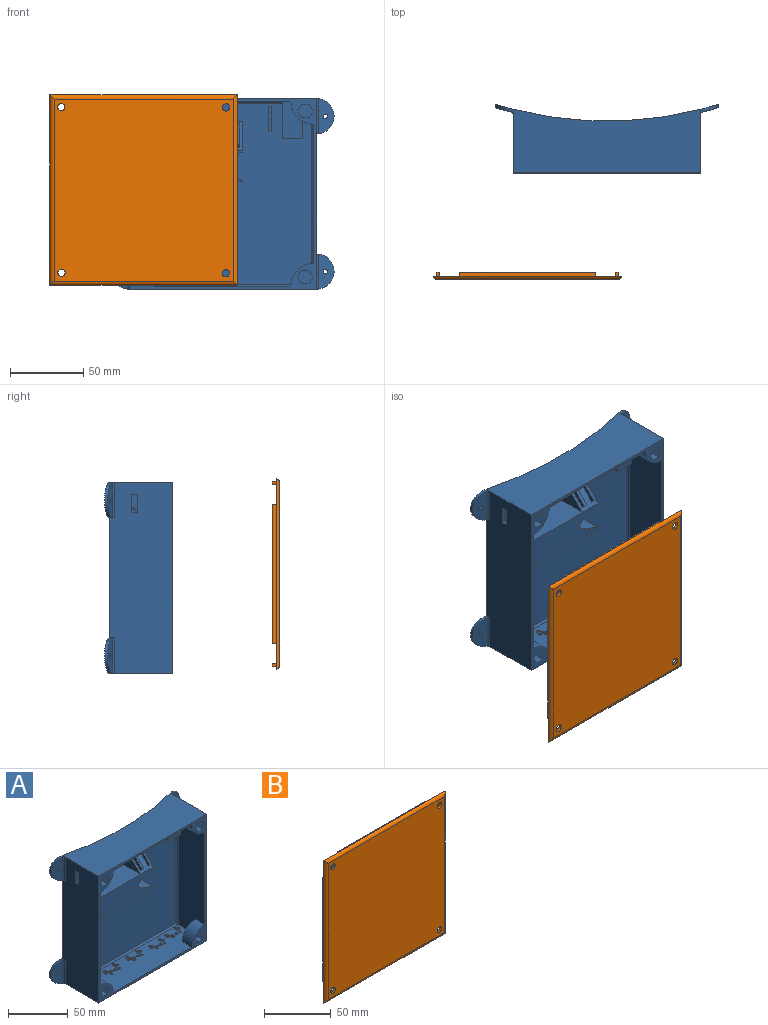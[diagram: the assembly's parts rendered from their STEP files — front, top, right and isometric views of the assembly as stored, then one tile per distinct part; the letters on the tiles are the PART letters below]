
ASSEMBLY  parts=2 mates=1
PART A: 159 faces, bbox 152x46.7x130 mm
  f0: plane 126x31.5mm, normal (1,0,0), area 3564.5mm2, adj f8,f10,f11,f21,f35,f36,f39,f40
  f1: plane 130x43.3mm, normal (-1,0,0), area 5426.5mm2, adj f8,f12,f13,f14,f17,f25,f31,f34
  f2: plane 70x21mm, normal (0,-1,0), area 1246mm2, adj f3,f130,f131,f132,f133,f137,f139
  f3: plane 21.01x20mm, normal (1,0,0), area 220mm2, adj f2,f4,f6,f136,f137,f139
  f4: plane 69x19mm, normal (0,0,-1), area 1310.4mm2, adj f3,f5,f6,f134,f136,f137
  f5: plane 69x19.04mm, normal (0,1,0), area 1087mm2, adj f4,f133,f134,f135,f137
  f6: plane 123x121mm, normal (0,-1,0), area 14390mm2, adj f3,f4,f21,f22,f23,f24,f125,f126
  f7: plane 130x43.3mm, normal (1,0,0), area 5424.5mm2, adj f8,f12,f13,f14,f15,f26,f29,f30
  f8: plane 130x128mm, normal (0,-1,0), area 1478.8mm2, adj f0,f1,f7,f9,f10,f11,f12,f13
  f9: plane 126x31.5mm, normal (-1,0,0), area 3577.1mm2, adj f8,f10,f11,f24,f37,f38,f41,f42
  f10: plane 124x31.5mm, normal (0,0,1), area 3271.1mm2, adj f0,f8,f9,f23,f39,f40,f41,f42
  f11: plane 124x31.5mm, normal (0,0,-1), area 3507.5mm2, adj f0,f8,f9,f22,f35,f36,f37,f38
  f12: plane 128x43.3mm, normal (0,0,1), area 4849.1mm2, adj f1,f7,f8,f14,f15,f17
  f13: plane 128x43.3mm, normal (0,0,-1), area 4849.1mm2, adj f1,f7,f8,f14,f30,f31
  f14: cylinder r=256.8mm len=152mm, axis (0,0,-1), area 17727.9mm2, adj f1,f7,f12,f13,f15,f17,f19,f20
  f15: cylinder r=12mm len=24mm, axis (0,1,0), area 79mm2, adj f7,f12,f14,f16,f26
  f16: cylinder r=258.8mm len=23.89mm, axis (0,0,-1), area 199.6mm2, adj f15,f19,f26
  f17: cylinder r=12mm len=24mm, axis (0,1,0), area 79mm2, adj f1,f12,f14,f18,f25
  f18: cylinder r=258.8mm len=23.89mm, axis (0,0,-1), area 199.6mm2, adj f17,f20,f25
  f19: cylinder r=1.5mm len=3mm, axis (0,1,0), area 19.6mm2, adj f14,f16
  f20: cylinder r=1.5mm len=3mm, axis (0,1,0), area 19.6mm2, adj f14,f18
  f21: cylinder r=1.5mm len=126mm, axis (0,0,1), area 294.3mm2, adj f0,f6,f22,f23
  f22: cylinder r=1.5mm len=124mm, axis (1,0,0), area 289.6mm2, adj f6,f11,f21,f24
  f23: cylinder r=1.5mm len=124mm, axis (-1,0,0), area 289.6mm2, adj f6,f10,f21,f24
  f24: cylinder r=1.5mm len=126mm, axis (0,0,-1), area 274.1mm2, adj f6,f9,f22,f23,f122,f123,f124
  f25: cylinder r=1.5mm len=24mm, axis (0,0,-1), area 47.3mm2, adj f1,f17,f18
  f26: cylinder r=1.5mm len=24mm, axis (0,0,-1), area 47.3mm2, adj f7,f15,f16
  f27: cylinder r=258.8mm len=23.89mm, axis (0,0,-1), area 199.6mm2, adj f28,f29,f30
  f28: cylinder r=1.5mm len=3mm, axis (0,1,0), area 19.6mm2, adj f14,f27
  f29: cylinder r=1.5mm len=24mm, axis (0,0,-1), area 47.3mm2, adj f7,f27,f30
  f30: cylinder r=12mm len=24mm, axis (0,1,0), area 79mm2, adj f7,f13,f14,f27,f29
  f31: cylinder r=12mm len=24mm, axis (0,1,0), area 79mm2, adj f1,f13,f14,f32,f34
  f32: cylinder r=258.8mm len=23.89mm, axis (0,0,-1), area 199.6mm2, adj f31,f33,f34
  f33: cylinder r=1.5mm len=3mm, axis (0,1,0), area 19.6mm2, adj f14,f32
  f34: cylinder r=1.5mm len=24mm, axis (0,0,-1), area 47.3mm2, adj f1,f31,f32
  f35: cylinder r=15.5mm len=15.5mm, axis (0,-1,0), area 280mm2, adj f0,f8,f11,f36
  f36: plane 15.5x15.5mm, normal (0,1,0), area 188.7mm2, adj f0,f11,f35
  f37: cylinder r=15.5mm len=15.5mm, axis (0,-1,0), area 280mm2, adj f8,f9,f11,f38
  f38: plane 15.5x15.5mm, normal (0,1,0), area 188.7mm2, adj f9,f11,f37
  f39: cylinder r=15.5mm len=15.5mm, axis (0,-1,0), area 280mm2, adj f0,f8,f10,f40
  f40: plane 15.5x15.5mm, normal (0,1,0), area 188.7mm2, adj f0,f10,f39
  f41: cylinder r=15.5mm len=15.5mm, axis (0,-1,0), area 280mm2, adj f8,f9,f10,f42
  f42: plane 15.5x15.5mm, normal (0,1,0), area 188.7mm2, adj f9,f10,f41
  f43: plane 9x5.3mm, normal (0,0,-1), area 47.7mm2, adj f8,f44,f48,f49
  f44: plane 9x4.59mm, normal (0.87,0,-0.5), area 47.7mm2, adj f8,f43,f45,f49
  f45: plane 9x4.59mm, normal (0.87,0,0.5), area 47.7mm2, adj f8,f44,f46,f49
  f46: plane 9x5.3mm, normal (0,0,1), area 47.7mm2, adj f8,f45,f47,f49
  f47: plane 9x4.59mm, normal (-0.87,0,0.5), area 47.7mm2, adj f8,f46,f48,f49
  f48: plane 9x4.59mm, normal (-0.87,0,-0.5), area 47.7mm2, adj f8,f43,f47,f49
  f49: plane 10.6x9.18mm, normal (0,-1,0), area 73mm2, adj f43,f44,f45,f46,f47,f48
  f50: plane 9x5.3mm, normal (0,0,-1), area 47.7mm2, adj f8,f51,f55,f56
  f51: plane 9x4.59mm, normal (0.87,0,-0.5), area 47.7mm2, adj f8,f50,f52,f56
  f52: plane 9x4.59mm, normal (0.87,0,0.5), area 47.7mm2, adj f8,f51,f53,f56
  f53: plane 9x5.3mm, normal (0,0,1), area 47.7mm2, adj f8,f52,f54,f56
  f54: plane 9x4.59mm, normal (-0.87,0,0.5), area 47.7mm2, adj f8,f53,f55,f56
  f55: plane 9x4.59mm, normal (-0.87,0,-0.5), area 47.7mm2, adj f8,f50,f54,f56
  f56: plane 10.6x9.18mm, normal (0,-1,0), area 73mm2, adj f50,f51,f52,f53,f54,f55
  f57: plane 9x4.59mm, normal (0.87,0,-0.5), area 47.7mm2, adj f8,f58,f62,f63
  f58: plane 9x4.59mm, normal (0.87,0,0.5), area 47.7mm2, adj f8,f57,f59,f63
  f59: plane 9x5.3mm, normal (0,0,1), area 47.7mm2, adj f8,f58,f60,f63
  f60: plane 9x4.59mm, normal (-0.87,0,0.5), area 47.7mm2, adj f8,f59,f61,f63
  f61: plane 9x4.59mm, normal (-0.87,0,-0.5), area 47.7mm2, adj f8,f60,f62,f63
  f62: plane 9x5.3mm, normal (0,0,-1), area 47.7mm2, adj f8,f57,f61,f63
  f63: plane 10.6x9.18mm, normal (0,-1,0), area 73mm2, adj f57,f58,f59,f60,f61,f62
  f64: plane 9x4.59mm, normal (0.87,0,-0.5), area 47.7mm2, adj f8,f65,f69,f70
  f65: plane 9x4.59mm, normal (0.87,0,0.5), area 47.7mm2, adj f8,f64,f66,f70
  f66: plane 9x5.3mm, normal (0,0,1), area 47.7mm2, adj f8,f65,f67,f70
  f67: plane 9x4.59mm, normal (-0.87,0,0.5), area 47.7mm2, adj f8,f66,f68,f70
  f68: plane 9x4.59mm, normal (-0.87,0,-0.5), area 47.7mm2, adj f8,f67,f69,f70
  f69: plane 9x5.3mm, normal (0,0,-1), area 47.7mm2, adj f8,f64,f68,f70
  f70: plane 10.6x9.18mm, normal (0,-1,0), area 73mm2, adj f64,f65,f66,f67,f68,f69
  f71: extruded ~2.04x1.93mm, area 6.2mm2, adj f10,f72,f74,f75
  f72: extruded ~3.6x2.54mm, area 4.5mm2, adj f10,f71,f73,f75
  f73: extruded ~1.97x1.68mm, area 4.8mm2, adj f10,f72,f74,f75
  f74: extruded ~8.28x7.2mm, area 19.6mm2, adj f10,f71,f73,f75
  f75: plane 9.34x8.79mm, normal (0,0,1), area 29.2mm2, adj f71,f72,f73,f74
  f76: extruded ~2.36x1.44mm, area 5mm2, adj f10,f77,f79,f80
  f77: extruded ~1.96x1.92mm, area 2.8mm2, adj f10,f76,f78,f80
  f78: extruded ~2.48x1.95mm, area 6.9mm2, adj f10,f77,f79,f80
  f79: extruded ~6.92x6.39mm, area 18.5mm2, adj f10,f76,f78,f80
  f80: plane 8.86x7.7mm, normal (0,0,1), area 26.5mm2, adj f76,f77,f78,f79
  f81: extruded ~2.04x1.93mm, area 6.2mm2, adj f10,f82,f84,f85
  f82: extruded ~3.6x2.54mm, area 4.5mm2, adj f10,f81,f83,f85
  f83: extruded ~1.97x1.68mm, area 4.8mm2, adj f10,f82,f84,f85
  f84: extruded ~8.28x7.2mm, area 19.6mm2, adj f10,f81,f83,f85
  f85: plane 9.34x8.79mm, normal (0,0,1), area 29.2mm2, adj f81,f82,f83,f84
  f86: extruded ~2.36x1.44mm, area 5mm2, adj f10,f87,f89,f90
  f87: extruded ~1.96x1.92mm, area 2.8mm2, adj f10,f86,f88,f90
  f88: extruded ~2.48x1.95mm, area 6.9mm2, adj f10,f87,f89,f90
  f89: extruded ~6.92x6.39mm, area 18.5mm2, adj f10,f86,f88,f90
  f90: plane 8.86x7.7mm, normal (0,0,1), area 26.5mm2, adj f86,f87,f88,f89
  f91: extruded ~2.04x1.93mm, area 6.2mm2, adj f10,f92,f94,f95
  f92: extruded ~3.6x2.54mm, area 4.5mm2, adj f10,f91,f93,f95
  f93: extruded ~1.97x1.68mm, area 4.8mm2, adj f10,f92,f94,f95
  f94: extruded ~8.28x7.2mm, area 19.6mm2, adj f10,f91,f93,f95
  f95: plane 9.34x8.79mm, normal (0,0,1), area 29.2mm2, adj f91,f92,f93,f94
  f96: extruded ~2.36x1.44mm, area 5mm2, adj f10,f97,f99,f100
  f97: extruded ~1.96x1.92mm, area 2.8mm2, adj f10,f96,f98,f100
  f98: extruded ~2.48x1.95mm, area 6.9mm2, adj f10,f97,f99,f100
  f99: extruded ~6.92x6.39mm, area 18.5mm2, adj f10,f96,f98,f100
  f100: plane 8.86x7.7mm, normal (0,0,1), area 26.5mm2, adj f96,f97,f98,f99
  f101: extruded ~2.04x1.93mm, area 6.2mm2, adj f10,f102,f104,f105
  f102: extruded ~3.6x2.54mm, area 4.5mm2, adj f10,f101,f103,f105
  f103: extruded ~1.97x1.68mm, area 4.8mm2, adj f10,f102,f104,f105
  f104: extruded ~8.28x7.2mm, area 19.6mm2, adj f10,f101,f103,f105
  f105: plane 9.34x8.79mm, normal (0,0,1), area 29.2mm2, adj f101,f102,f103,f104
  f106: extruded ~2.36x1.44mm, area 5mm2, adj f10,f107,f109,f110
  f107: extruded ~1.96x1.92mm, area 2.8mm2, adj f10,f106,f108,f110
  f108: extruded ~2.48x1.95mm, area 6.9mm2, adj f10,f107,f109,f110
  f109: extruded ~6.92x6.39mm, area 18.5mm2, adj f10,f106,f108,f110
  f110: plane 8.86x7.7mm, normal (0,0,1), area 26.5mm2, adj f106,f107,f108,f109
  f111: extruded ~2.04x1.93mm, area 6.2mm2, adj f10,f112,f114,f115
  f112: extruded ~3.6x2.54mm, area 4.5mm2, adj f10,f111,f113,f115
  f113: extruded ~1.97x1.68mm, area 4.8mm2, adj f10,f112,f114,f115
  f114: extruded ~8.28x7.2mm, area 19.6mm2, adj f10,f111,f113,f115
  f115: plane 9.34x8.79mm, normal (0,0,1), area 29.2mm2, adj f111,f112,f113,f114
  f116: extruded ~1.96x1.92mm, area 2.8mm2, adj f10,f117,f119,f120
  f117: extruded ~2.48x1.95mm, area 6.9mm2, adj f10,f116,f118,f120
  f118: extruded ~6.92x6.39mm, area 18.5mm2, adj f10,f117,f119,f120
  f119: extruded ~2.36x1.44mm, area 5mm2, adj f10,f116,f118,f120
  f120: plane 8.86x7.7mm, normal (0,0,1), area 26.5mm2, adj f116,f117,f118,f119
  f121: plane 10x2mm, normal (0,1,0), area 20mm2, adj f7,f9,f123,f124
  f122: plane 10x3.17mm, normal (0,-1,0), area 31.7mm2, adj f7,f24,f123,f124
  f123: plane 5x3.17mm, normal (0,0,-1), area 10.4mm2, adj f7,f9,f24,f121,f122
  f124: plane 5x3.17mm, normal (0,0,1), area 10.4mm2, adj f7,f9,f24,f121,f122
  f125: plane 5x2mm, normal (0,0,-1), area 10mm2, adj f6,f126,f128,f129
  f126: plane 17x5mm, normal (1,0,0), area 85mm2, adj f6,f125,f127,f129
  f127: plane 5x2mm, normal (0,0,1), area 10mm2, adj f6,f126,f128,f129
  f128: plane 17x5mm, normal (-1,0,0), area 85mm2, adj f6,f125,f127,f129
  f129: plane 17x2mm, normal (0,-1,0), area 34mm2, adj f125,f126,f127,f128
  f130: plane 55x20mm, normal (0,0,1), area 1100mm2, adj f2,f6,f131,f138
  f131: plane 21x20mm, normal (-1,0,0), area 420mm2, adj f2,f6,f130,f132
  f132: plane 70x20mm, normal (0,0,-1), area 1400mm2, adj f2,f6,f131,f133
  f133: plane 20x1.03mm, normal (1,0,0), area 19.8mm2, adj f2,f5,f6,f132,f135,f137
  f134: plane 19x19mm, normal (1,0,0), area 361mm2, adj f4,f5,f6,f135
  f135: plane 69x19mm, normal (0,0,1), area 1311mm2, adj f5,f6,f133,f134
  f136: plane 0.14x0.04mm, normal (0,-1,0), area 0mm2, adj f3,f4,f137
  f137: extruded ~18.99x17.69mm, area 42.4mm2, adj f2,f3,f4,f5,f133,f136
  f138: plane 20x20mm, normal (-1,0,0), area 200mm2, adj f6,f130,f139
  f139: plane 20x20mm, normal (0,-0.71,0.71), area 344.5mm2, adj f2,f3,f6,f138,f140,f141,f142,f143
  f140: plane 16.26x16.26mm, normal (-1,0,0), area 60mm2, adj f139,f141,f143,f144
  f141: plane 2.12x2.12mm, normal (0,-0.71,-0.71), area 6mm2, adj f139,f140,f142,f144
  f142: plane 16.26x16.26mm, normal (1,0,0), area 60mm2, adj f139,f141,f143,f144
  f143: plane 2.12x2.12mm, normal (0,0.71,0.71), area 6mm2, adj f139,f140,f142,f144
  f144: plane 14.14x14.14mm, normal (0,-0.71,0.71), area 40mm2, adj f140,f141,f142,f143
  f145: plane 2.12x2.12mm, normal (0,-0.71,-0.71), area 6mm2, adj f139,f146,f148,f149
  f146: plane 16.19x16.19mm, normal (1,0,0), area 59.7mm2, adj f139,f145,f147,f149
  f147: plane 2.12x2.12mm, normal (0,0.71,0.71), area 6mm2, adj f139,f146,f148,f149
  f148: plane 16.19x16.19mm, normal (-1,0,0), area 59.7mm2, adj f139,f145,f147,f149
  f149: plane 14.07x14.07mm, normal (0,-0.71,0.71), area 39.8mm2, adj f145,f146,f147,f148
  f150: plane 25x14mm, normal (0,-1,0), area 350mm2, adj f11,f151,f153,f154
  f151: plane 25x3mm, normal (-1,0,0), area 75mm2, adj f11,f150,f152,f154
  f152: plane 25x14mm, normal (0,1,0), area 350mm2, adj f11,f151,f153,f154
  f153: plane 25x3mm, normal (1,0,0), area 75mm2, adj f11,f150,f152,f154
  f154: plane 14x3mm, normal (0,0,-1), area 42mm2, adj f150,f151,f152,f153
  f155: plane 4x2mm, normal (0,0,-1), area 8mm2, adj f0,f1,f156,f158
  f156: plane 12x2mm, normal (0,1,0), area 24mm2, adj f0,f1,f155,f157
  f157: plane 4x2mm, normal (0,0,1), area 8mm2, adj f0,f1,f156,f158
  f158: plane 12x2mm, normal (0,-1,0), area 24mm2, adj f0,f1,f155,f157
PART B: 30 faces, bbox 128x5x130 mm
  f0: plane 130x128mm, normal (0,1,0), area 15809.5mm2, adj f2,f3,f4,f5,f6,f7,f8,f9
  f1: plane 124.34x122.34mm, normal (0,-1,0), area 15134mm2, adj f2,f3,f4,f5,f6,f7,f8,f9
  f2: cylinder r=2.5mm len=5mm, axis (0,-1,0), area 31.4mm2, adj f0,f1
  f3: cylinder r=2.5mm len=5mm, axis (0,-1,0), area 31.4mm2, adj f0,f1
  f4: cylinder r=2.5mm len=5mm, axis (0,-1,0), area 31.4mm2, adj f0,f1
  f5: cylinder r=2.5mm len=5mm, axis (0,-1,0), area 31.4mm2, adj f0,f1
  f6: cylinder r=3mm len=128mm, axis (1,0,0), area 463.8mm2, adj f0,f1,f7,f8
  f7: cylinder r=3mm len=130mm, axis (0,0,-1), area 471.2mm2, adj f0,f1,f6,f9
  f8: cylinder r=3mm len=130mm, axis (0,0,-1), area 471.2mm2, adj f0,f1,f6,f9
  f9: cylinder r=3mm len=128mm, axis (1,0,0), area 463.8mm2, adj f0,f1,f7,f8
  f10: plane 95x3mm, normal (1,0,0), area 285mm2, adj f0,f11,f13,f14
  f11: plane 3x2mm, normal (0,0,-1), area 6mm2, adj f0,f10,f12,f14
  f12: plane 95x3mm, normal (-1,0,0), area 285mm2, adj f0,f11,f13,f14
  f13: plane 3x2mm, normal (0,0,1), area 6mm2, adj f0,f10,f12,f14
  f14: plane 95x2mm, normal (0,1,0), area 190mm2, adj f10,f11,f12,f13
  f15: plane 3x2mm, normal (1,0,0), area 6mm2, adj f0,f16,f18,f19
  f16: plane 93x3mm, normal (0,0,-1), area 279mm2, adj f0,f15,f17,f19
  f17: plane 3x2mm, normal (-1,0,0), area 6mm2, adj f0,f16,f18,f19
  f18: plane 93x3mm, normal (0,0,1), area 279mm2, adj f0,f15,f17,f19
  f19: plane 93x2mm, normal (0,1,0), area 186mm2, adj f15,f16,f17,f18
  f20: plane 3x2mm, normal (0,0,-1), area 6mm2, adj f0,f21,f23,f24
  f21: plane 95x3mm, normal (-1,0,0), area 285mm2, adj f0,f20,f22,f24
  f22: plane 3x2mm, normal (0,0,1), area 6mm2, adj f0,f21,f23,f24
  f23: plane 95x3mm, normal (1,0,0), area 285mm2, adj f0,f20,f22,f24
  f24: plane 95x2mm, normal (0,1,0), area 190mm2, adj f20,f21,f22,f23
  f25: plane 93x3mm, normal (0,0,1), area 279mm2, adj f0,f26,f28,f29
  f26: plane 3x2mm, normal (1,0,0), area 6mm2, adj f0,f25,f27,f29
  f27: plane 93x3mm, normal (0,0,-1), area 279mm2, adj f0,f26,f28,f29
  f28: plane 3x2mm, normal (-1,0,0), area 6mm2, adj f0,f25,f27,f29
  f29: plane 93x2mm, normal (0,1,0), area 186mm2, adj f25,f26,f27,f28
PLACE A rot(axis=(0.71,0.71,0.07),0deg) t=(-34.64,54.83,-30.92)mm
PLACE B rot(axis=(0.71,0.71,0.07),0deg) t=(-88.75,-0.98,-28.25)mm
MATE parallel A.f8 <-> B.f0  axis (0,-1,0) through (-98.64,19.83,34.08)mm
